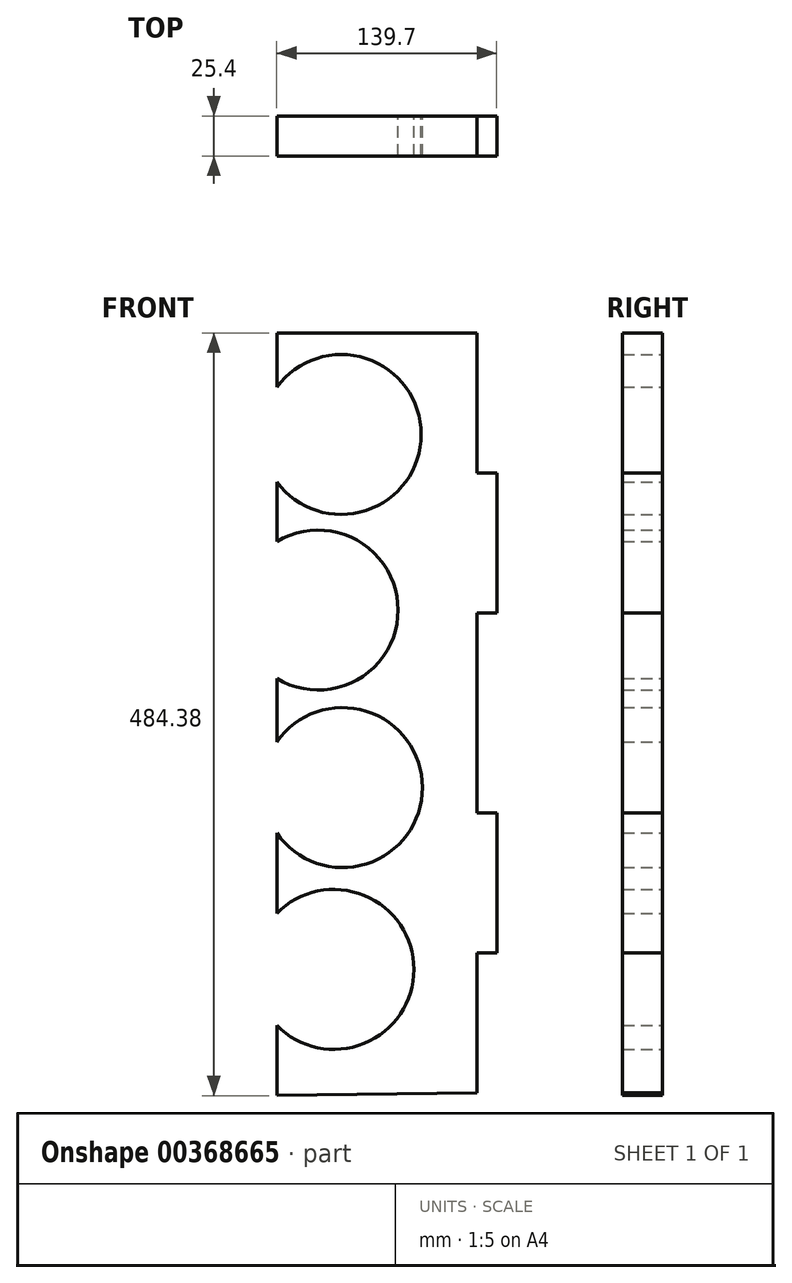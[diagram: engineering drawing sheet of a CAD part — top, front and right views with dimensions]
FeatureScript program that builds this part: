
annotation { "Feature Type Name" : "Feature", "Feature Type Description" : "" }
export const myFeature = defineFeature(function(context is Context, id is Id, definition is map)
    precondition{}
    {
        {
            var Q0;
            Q0=qCreatedBy(makeId("Front.planeOp"),FACE);
            var sketch = newSketch(context, id + "F0", { "sketchPlane" : qUnion([Q0])});
            skLineSegment(sketch, "E0", {"start": v(59.92, 308.28) * mm, "end": v(-67.08, 308.28) * mm});
            skArc(sketch, "E1", {"start": v(-67.08, 213.7) * mm, "mid": v(24.63, 243.8) * mm, "end": v(-67.08, 273.93) * mm});
            skArc(sketch, "E2", {"start": v(-67.08, 88.77) * mm, "mid": v(9.95, 132.27) * mm, "end": v(-67.08, 175.78) * mm});
            skArc(sketch, "E3", {"start": v(-67.08, -9.38) * mm, "mid": v(25.48, 19.55) * mm, "end": v(-67.08, 48.48) * mm});
            skArc(sketch, "E4", {"start": v(-67.08, -131.53) * mm, "mid": v(19.99, -95.96) * mm, "end": v(-67.08, -60.38) * mm});
            skLineSegment(sketch, "E5", {"start": v(59.92, 308.28) * mm, "end": v(59.92, -174.32) * mm});
            skLineSegment(sketch, "E6", {"start": v(-67.08, -176.1) * mm, "end": v(59.92, -174.32) * mm});
            skLineSegment(sketch, "E7", {"start": v(-67.08, 308.28) * mm, "end": v(-67.08, 273.93) * mm});
            skLineSegment(sketch, "E8", {"start": v(-67.08, 213.7) * mm, "end": v(-67.08, 175.78) * mm});
            skLineSegment(sketch, "E9", {"start": v(-67.08, 88.77) * mm, "end": v(-67.08, 48.48) * mm});
            skLineSegment(sketch, "E10", {"start": v(-67.08, -9.38) * mm, "end": v(-67.08, -60.38) * mm});
            skLineSegment(sketch, "E11", {"start": v(-67.08, -131.53) * mm, "end": v(-67.08, -176.1) * mm});
            skLineSegment(sketch, "E12.top", {"start": v(59.92, -85.42) * mm, "end": v(72.62, -85.42) * mm});
            skLineSegment(sketch, "E12.left", {"start": v(59.92, -3.23) * mm, "end": v(59.92, -85.42) * mm});
            skLineSegment(sketch, "E13", {"start": v(72.62, -85.42) * mm, "end": v(72.62, 3.48) * mm});
            skLineSegment(sketch, "E14", {"start": v(72.62, 3.48) * mm, "end": v(59.92, 3.48) * mm});
            skLineSegment(sketch, "E15", {"start": v(72.62, 219.38) * mm, "end": v(59.92, 219.38) * mm});
            skLineSegment(sketch, "E16", {"start": v(72.62, 219.38) * mm, "end": v(72.62, 130.48) * mm});
            skLineSegment(sketch, "E17", {"start": v(72.62, 130.48) * mm, "end": v(59.92, 130.48) * mm});
            skSolve(sketch);
        }
        {
            var Q0;
            Q0 = qSketchRegion(id + "F0", true);
            extrude(context, id + "F1", {"entities" : qUnion([Q0]), "depth" : 12.7 * mm});
        }
        {
            var Q0;
            Q0=makeQuery(id+"F1.opExtrude","CAP_FACE",FACE,{"disambiguationData":[OSD([sQuery(id+"F0.wireOp",EDGE,"E0"),sQuery(id+"F0.wireOp",EDGE,"E1"),sQuery(id+"F0.wireOp",EDGE,"E2"),sQuery(id+"F0.wireOp",EDGE,"E3"),sQuery(id+"F0.wireOp",EDGE,"E4"),sQuery(id+"F0.wireOp",EDGE,"E5"),sQuery(id+"F0.wireOp",EDGE,"E6"),sQuery(id+"F0.wireOp",EDGE,"E7"),sQuery(id+"F0.wireOp",EDGE,"E8"),sQuery(id+"F0.wireOp",EDGE,"E9"),sQuery(id+"F0.wireOp",EDGE,"E10"),sQuery(id+"F0.wireOp",EDGE,"E11")])],"isStart":true});
            extrude(context, id + "F2", {"entities" : qUnion([Q0]), "operationType" : NewBodyOperationType.ADD, "depth" : 12.7 * mm});
        }
    });
